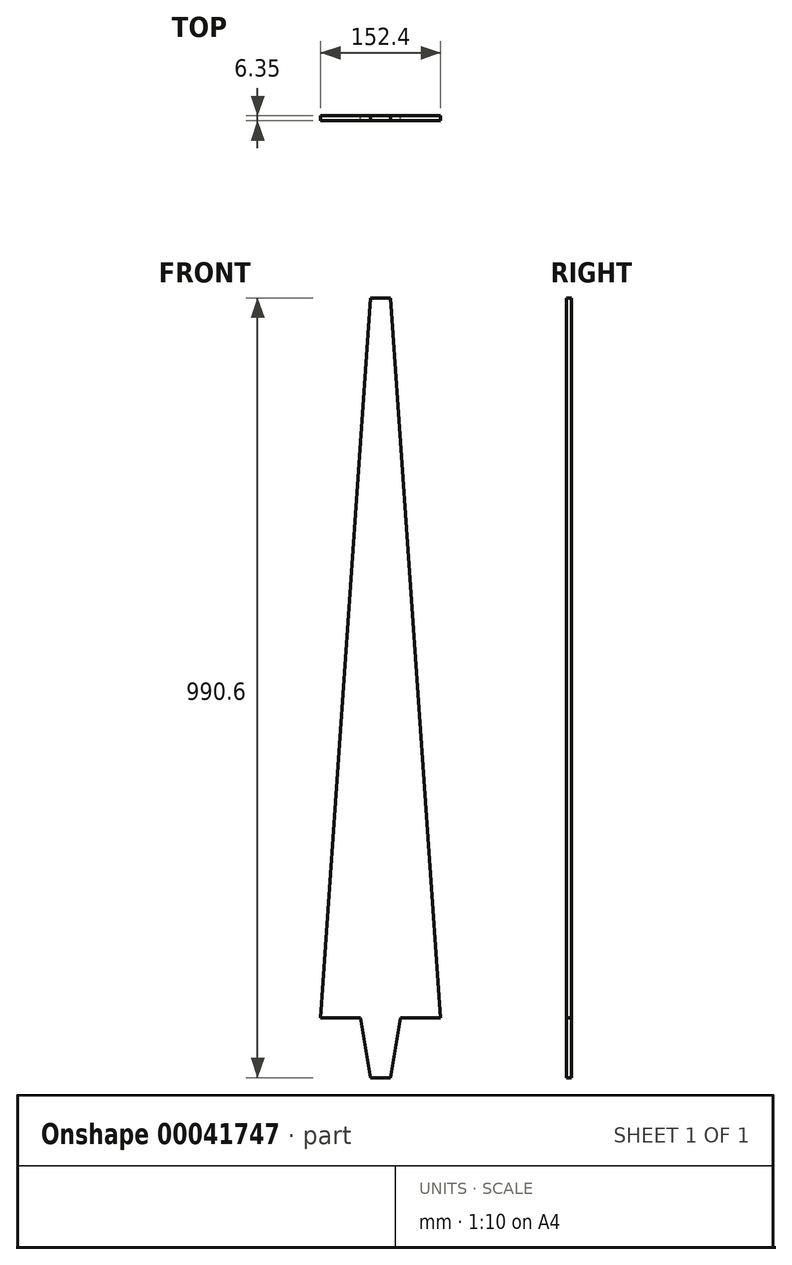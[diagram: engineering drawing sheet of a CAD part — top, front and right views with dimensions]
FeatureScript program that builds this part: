
annotation { "Feature Type Name" : "Feature", "Feature Type Description" : "" }
export const myFeature = defineFeature(function(context is Context, id is Id, definition is map)
    precondition{}
    {
        {
            var Q0;
            Q0=qCreatedBy(makeId("Front.planeOp"),FACE);
            var sketch = newSketch(context, id + "F0", { "sketchPlane" : qUnion([Q0])});
            skLineSegment(sketch, "E0", {"start": v(0, 877.34) * mm, "end": v(-12.7, 877.34) * mm});
            skLineSegment(sketch, "E1", {"start": v(-12.7, 877.34) * mm, "end": v(-76.2, -37.06) * mm});
            skLineSegment(sketch, "E2", {"start": v(-76.2, -37.06) * mm, "end": v(0, -37.06) * mm});
            skLineSegment(sketch, "E3", {"start": v(0, -37.06) * mm, "end": v(0, 877.34) * mm});
            skLineSegment(sketch, "E4", {"start": v(-25.4, -37.06) * mm, "end": v(-12.7, -113.26) * mm});
            skLineSegment(sketch, "E5", {"start": v(-12.7, -113.26) * mm, "end": v(0, -113.26) * mm});
            skLineSegment(sketch, "E6", {"start": v(0, -113.26) * mm, "end": v(0, -37.06) * mm});
            skLineSegment(sketch, "E7.MirrorCS", {"start": v(12.7, 877.34) * mm, "end": v(76.2, -37.06) * mm});
            skLineSegment(sketch, "E8.MirrorCS", {"start": v(76.2, -37.06) * mm, "end": v(0, -37.06) * mm});
            skLineSegment(sketch, "E9.MirrorCS", {"start": v(25.4, -37.06) * mm, "end": v(12.7, -113.26) * mm});
            skLineSegment(sketch, "E10.MirrorCS", {"start": v(12.7, -113.26) * mm, "end": v(0, -113.26) * mm});
            skLineSegment(sketch, "E11.MirrorCS", {"start": v(0, 877.34) * mm, "end": v(12.7, 877.34) * mm});
            skSolve(sketch);
        }
        {
            var Q0;
            Q0 = qSketchRegion(id + "F0", true);
            extrude(context, id + "F1", {"entities" : qUnion([Q0]), "depth" : 6.35 * mm});
        }
    });
